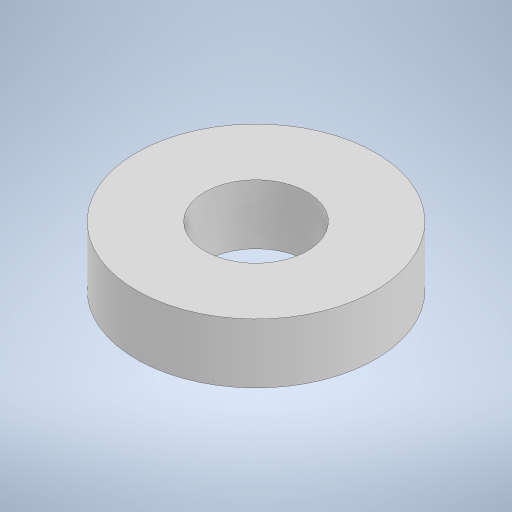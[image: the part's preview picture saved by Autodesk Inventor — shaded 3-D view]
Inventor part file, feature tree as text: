
AUTODESK INVENTOR PART (.ipt)
format: ipt  version: 2023 (Build 270158000, 158)  size: 201,728 bytes
history: native  units: mm
features: extrude x1, sketch x1
ambient origin geometry x8: Origin, YZ Plane, XZ Plane, XY Plane, X Axis, Y Axis, Z Axis, Center Point
bodies: Solid1 (feature_tree)
feature tree (2):
  extrude  "Extrusion1"  Depth=7.0mm
  sketch  "Sketch1"  dims[d0=12.0mm d1=28.0mm d2=7.0mm d3=0.0mm]
